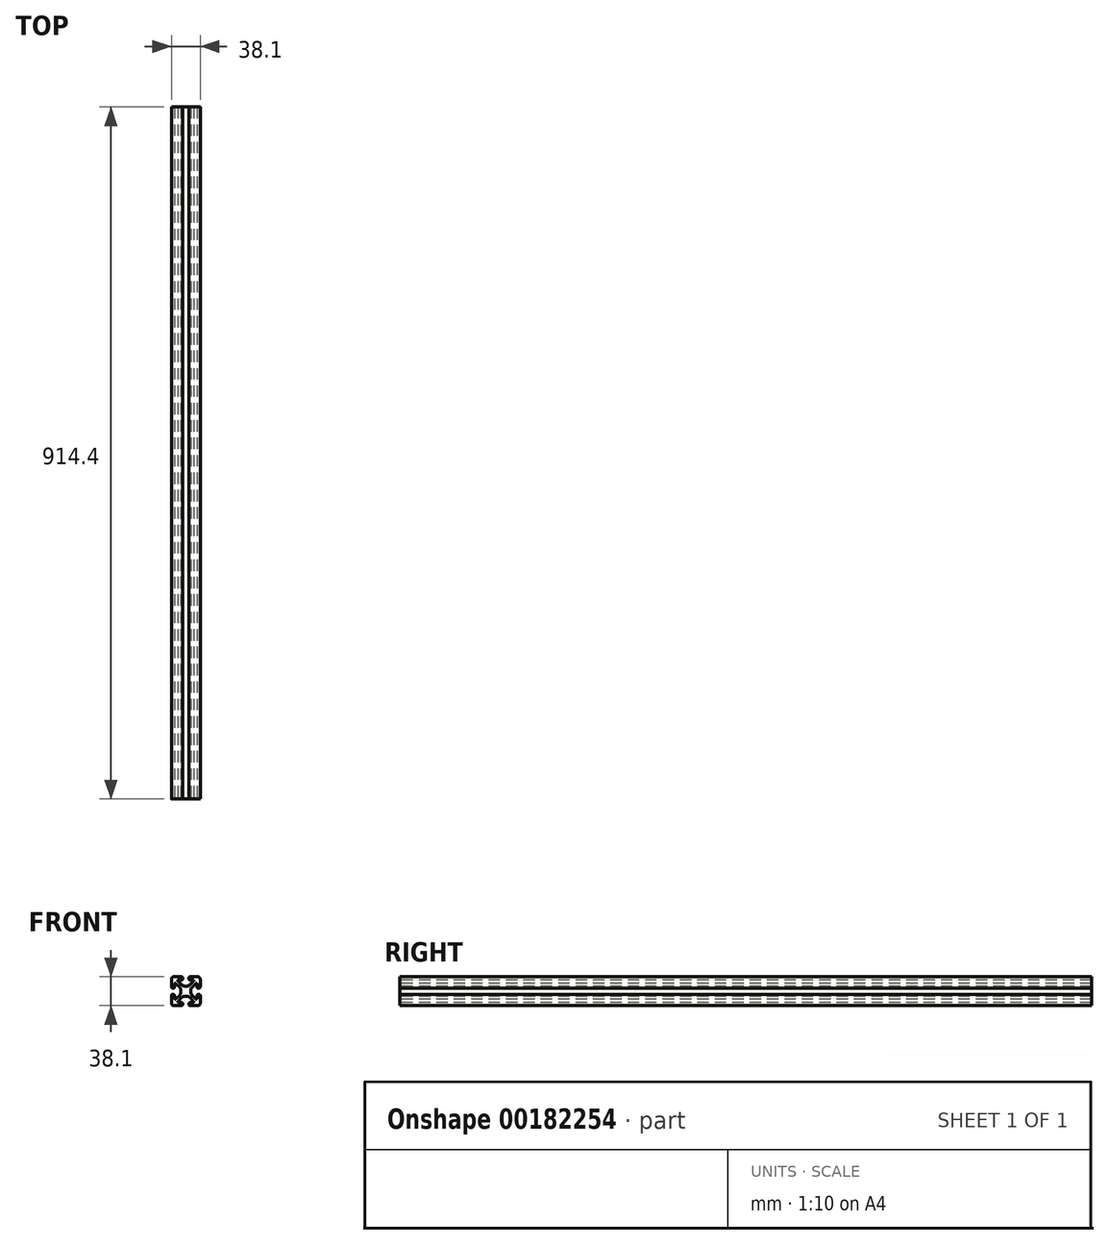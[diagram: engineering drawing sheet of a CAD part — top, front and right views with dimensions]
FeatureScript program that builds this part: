
annotation { "Feature Type Name" : "Feature", "Feature Type Description" : "" }
export const myFeature = defineFeature(function(context is Context, id is Id, definition is map)
    precondition{}
    {
        {
            var Q0;
            Q0=qCreatedBy(makeId("Front.planeOp"),FACE);
            var sketch = newSketch(context, id + "F0", { "sketchPlane" : qUnion([Q0])});
            skLineSegment(sketch, "E0", {"start": v(-16.03, 19.4) * mm, "end": v(-5.8, 19.4) * mm});
            skLineSegment(sketch, "E1.0", {"start": v(-19.2, 16.23) * mm, "end": v(-19.2, 5.99) * mm});
            skArc(sketch, "E2.0", {"start": v(-16.03, 19.4) * mm, "mid": v(-18.28, 18.47) * mm, "end": v(-19.2, 16.23) * mm});
            skArc(sketch, "E3.0", {"start": v(-19.2, 5.99) * mm, "mid": v(-18.75, 4.88) * mm, "end": v(-17.63, 4.41) * mm});
            skLineSegment(sketch, "E4.0", {"start": v(-17.63, 4.41) * mm, "end": v(-16.72, 4.41) * mm});
            skArc(sketch, "E5.0", {"start": v(-16.72, 4.41) * mm, "mid": v(-15.6, 4.88) * mm, "end": v(-15.15, 5.99) * mm});
            skLineSegment(sketch, "E6.0", {"start": v(-15.15, 5.99) * mm, "end": v(-15.15, 9.75) * mm});
            skArc(sketch, "E7.0", {"start": v(-15.15, 9.75) * mm, "mid": v(-14.89, 10.38) * mm, "end": v(-14.26, 10.64) * mm});
            skLineSegment(sketch, "E8.0", {"start": v(-14.26, 10.64) * mm, "end": v(-13.69, 10.64) * mm});
            skArc(sketch, "E9.0", {"start": v(-13.69, 10.64) * mm, "mid": v(-13.35, 10.57) * mm, "end": v(-13.06, 10.38) * mm});
            skLineSegment(sketch, "E10.0", {"start": v(-13.06, 10.38) * mm, "end": v(-8.42, 5.74) * mm});
            skArc(sketch, "E11.0", {"start": v(-8.42, 5.74) * mm, "mid": v(-7.4, 4.2) * mm, "end": v(-7.03, 2.38) * mm});
            skLineSegment(sketch, "E12.0", {"start": v(-7.03, 2.38) * mm, "end": v(-7.03, -1.68) * mm});
            skArc(sketch, "E13.0", {"start": v(-7.03, -1.68) * mm, "mid": v(-7.4, -3.5) * mm, "end": v(-8.42, -5.04) * mm});
            skLineSegment(sketch, "E14.0", {"start": v(-8.42, -5.04) * mm, "end": v(-13.06, -9.68) * mm});
            skArc(sketch, "E15.0", {"start": v(-13.06, -9.68) * mm, "mid": v(-13.35, -9.87) * mm, "end": v(-13.69, -9.94) * mm});
            skLineSegment(sketch, "E16.0", {"start": v(-13.69, -9.94) * mm, "end": v(-14.26, -9.94) * mm});
            skArc(sketch, "E17.0", {"start": v(-14.26, -9.94) * mm, "mid": v(-14.89, -9.68) * mm, "end": v(-15.15, -9.05) * mm});
            skLineSegment(sketch, "E18.0", {"start": v(-15.15, -9.05) * mm, "end": v(-15.15, -5.29) * mm});
            skArc(sketch, "E19.0", {"start": v(-15.15, -5.29) * mm, "mid": v(-15.6, -4.17) * mm, "end": v(-16.72, -3.71) * mm});
            skLineSegment(sketch, "E20.0", {"start": v(-16.72, -3.71) * mm, "end": v(-17.63, -3.71) * mm});
            skArc(sketch, "E21.0", {"start": v(-17.63, -3.71) * mm, "mid": v(-18.75, -4.17) * mm, "end": v(-19.2, -5.29) * mm});
            skLineSegment(sketch, "E22.0", {"start": v(-19.2, -5.29) * mm, "end": v(-19.2, -15.52) * mm});
            skArc(sketch, "E23.0", {"start": v(-19.2, -15.52) * mm, "mid": v(-18.28, -17.77) * mm, "end": v(-16.03, -18.7) * mm});
            skLineSegment(sketch, "E24.0", {"start": v(-16.03, -18.7) * mm, "end": v(-5.8, -18.7) * mm});
            skArc(sketch, "E25.0", {"start": v(-5.8, -18.7) * mm, "mid": v(-4.68, -18.24) * mm, "end": v(-4.22, -17.12) * mm});
            skLineSegment(sketch, "E26.0", {"start": v(-4.22, -17.12) * mm, "end": v(-4.22, -16.2) * mm});
            skArc(sketch, "E27.0", {"start": v(-4.22, -16.2) * mm, "mid": v(-4.68, -15.1) * mm, "end": v(-5.8, -14.64) * mm});
            skLineSegment(sketch, "E28.0", {"start": v(-5.8, -14.64) * mm, "end": v(-9.56, -14.64) * mm});
            skArc(sketch, "E29.0", {"start": v(-9.56, -14.64) * mm, "mid": v(-10.19, -14.37) * mm, "end": v(-10.45, -13.75) * mm});
            skLineSegment(sketch, "E30.0", {"start": v(-10.45, -13.75) * mm, "end": v(-10.45, -13.18) * mm});
            skArc(sketch, "E31.0", {"start": v(-10.45, -13.18) * mm, "mid": v(-10.38, -12.84) * mm, "end": v(-10.19, -12.55) * mm});
            skLineSegment(sketch, "E32.0", {"start": v(-10.19, -12.55) * mm, "end": v(-5.55, -7.91) * mm});
            skArc(sketch, "E33.0", {"start": v(-5.55, -7.91) * mm, "mid": v(-4, -6.88) * mm, "end": v(-2.19, -6.52) * mm});
            skLineSegment(sketch, "E34.0", {"start": v(-2.19, -6.52) * mm, "end": v(1.87, -6.52) * mm});
            skArc(sketch, "E35.0", {"start": v(1.87, -6.52) * mm, "mid": v(3.69, -6.88) * mm, "end": v(5.23, -7.91) * mm});
            skLineSegment(sketch, "E36.0", {"start": v(5.23, -7.91) * mm, "end": v(9.87, -12.55) * mm});
            skArc(sketch, "E37.0", {"start": v(9.87, -12.55) * mm, "mid": v(10.06, -12.84) * mm, "end": v(10.13, -13.18) * mm});
            skPoint(sketch, "E38.0", {"position": v(10.13, -13.75) * mm});
            skArc(sketch, "E39.0", {"start": v(10.13, -13.75) * mm, "mid": v(9.87, -14.37) * mm, "end": v(9.24, -14.64) * mm});
            skLineSegment(sketch, "E40.0", {"start": v(9.24, -14.64) * mm, "end": v(5.48, -14.64) * mm});
            skArc(sketch, "E41.0", {"start": v(5.48, -14.64) * mm, "mid": v(4.37, -15.1) * mm, "end": v(3.9, -16.2) * mm});
            skPoint(sketch, "E42.0", {"position": v(3.9, -17.12) * mm});
            skLineSegment(sketch, "E43.0", {"start": v(3.9, -16.2) * mm, "end": v(3.9, -17.12) * mm});
            skArc(sketch, "E44.0", {"start": v(3.9, -17.12) * mm, "mid": v(4.37, -18.24) * mm, "end": v(5.48, -18.7) * mm});
            skLineSegment(sketch, "E45.0", {"start": v(5.48, -18.7) * mm, "end": v(15.72, -18.7) * mm});
            skArc(sketch, "E46.0", {"start": v(15.72, -18.7) * mm, "mid": v(17.96, -17.77) * mm, "end": v(18.9, -15.52) * mm});
            skLineSegment(sketch, "E47.0", {"start": v(18.9, -15.52) * mm, "end": v(18.9, -5.29) * mm});
            skArc(sketch, "E48.0", {"start": v(18.9, -5.29) * mm, "mid": v(18.43, -4.17) * mm, "end": v(17.32, -3.71) * mm});
            skLineSegment(sketch, "E49.0", {"start": v(17.32, -3.71) * mm, "end": v(16.4, -3.71) * mm});
            skArc(sketch, "E50.0", {"start": v(16.4, -3.71) * mm, "mid": v(15.29, -4.17) * mm, "end": v(14.83, -5.29) * mm});
            skLineSegment(sketch, "E51.0", {"start": v(14.83, -5.29) * mm, "end": v(14.83, -9.05) * mm});
            skArc(sketch, "E52.0", {"start": v(14.83, -9.05) * mm, "mid": v(14.57, -9.68) * mm, "end": v(13.94, -9.94) * mm});
            skLineSegment(sketch, "E53.0", {"start": v(13.94, -9.94) * mm, "end": v(13.37, -9.94) * mm});
            skArc(sketch, "E54.0", {"start": v(13.37, -9.94) * mm, "mid": v(13.03, -9.87) * mm, "end": v(12.74, -9.68) * mm});
            skLineSegment(sketch, "E55.0", {"start": v(12.74, -9.68) * mm, "end": v(8.1, -5.04) * mm});
            skArc(sketch, "E56.0", {"start": v(8.1, -5.04) * mm, "mid": v(7.07, -3.5) * mm, "end": v(6.71, -1.68) * mm});
            skLineSegment(sketch, "E57.0", {"start": v(6.71, -1.68) * mm, "end": v(6.71, 2.38) * mm});
            skArc(sketch, "E58.0", {"start": v(6.71, 2.38) * mm, "mid": v(7.07, 4.2) * mm, "end": v(8.1, 5.74) * mm});
            skLineSegment(sketch, "E59.0", {"start": v(8.1, 5.74) * mm, "end": v(12.74, 10.38) * mm});
            skArc(sketch, "E60.0", {"start": v(12.74, 10.38) * mm, "mid": v(13.03, 10.57) * mm, "end": v(13.37, 10.64) * mm});
            skLineSegment(sketch, "E61.0", {"start": v(13.37, 10.64) * mm, "end": v(13.94, 10.64) * mm});
            skArc(sketch, "E62.0", {"start": v(13.94, 10.64) * mm, "mid": v(14.57, 10.38) * mm, "end": v(14.83, 9.75) * mm});
            skLineSegment(sketch, "E63.0", {"start": v(14.83, 9.75) * mm, "end": v(14.83, 5.99) * mm});
            skArc(sketch, "E64.0", {"start": v(14.83, 5.99) * mm, "mid": v(15.29, 4.88) * mm, "end": v(16.4, 4.41) * mm});
            skLineSegment(sketch, "E65.0", {"start": v(16.4, 4.41) * mm, "end": v(17.32, 4.41) * mm});
            skArc(sketch, "E66.0", {"start": v(17.32, 4.41) * mm, "mid": v(18.43, 4.88) * mm, "end": v(18.9, 5.99) * mm});
            skLineSegment(sketch, "E67.0", {"start": v(18.9, 5.99) * mm, "end": v(18.9, 16.23) * mm});
            skArc(sketch, "E68.0", {"start": v(18.9, 16.23) * mm, "mid": v(17.96, 18.47) * mm, "end": v(15.72, 19.4) * mm});
            skLineSegment(sketch, "E69.0", {"start": v(15.72, 19.4) * mm, "end": v(5.48, 19.4) * mm});
            skArc(sketch, "E70.0", {"start": v(5.48, 19.4) * mm, "mid": v(4.37, 18.94) * mm, "end": v(3.9, 17.83) * mm});
            skLineSegment(sketch, "E71.0", {"start": v(3.9, 17.83) * mm, "end": v(3.9, 16.91) * mm});
            skArc(sketch, "E72.0", {"start": v(3.9, 16.91) * mm, "mid": v(4.37, 15.8) * mm, "end": v(5.48, 15.34) * mm});
            skLineSegment(sketch, "E73.0", {"start": v(5.48, 15.34) * mm, "end": v(9.24, 15.34) * mm});
            skArc(sketch, "E74.0", {"start": v(9.24, 15.34) * mm, "mid": v(9.87, 15.08) * mm, "end": v(10.13, 14.45) * mm});
            skLineSegment(sketch, "E75.0", {"start": v(10.13, 14.45) * mm, "end": v(10.13, 13.88) * mm});
            skArc(sketch, "E76.0", {"start": v(10.13, 13.88) * mm, "mid": v(10.06, 13.54) * mm, "end": v(9.87, 13.25) * mm});
            skLineSegment(sketch, "E77.0", {"start": v(9.87, 13.25) * mm, "end": v(5.23, 8.61) * mm});
            skArc(sketch, "E78.0", {"start": v(-4.22, 17.83) * mm, "mid": v(-4.68, 18.94) * mm, "end": v(-5.8, 19.4) * mm});
            skLineSegment(sketch, "E79.0", {"start": v(-4.22, 16.91) * mm, "end": v(-4.22, 17.83) * mm});
            skArc(sketch, "E80.0", {"start": v(-5.8, 15.34) * mm, "mid": v(-4.68, 15.8) * mm, "end": v(-4.22, 16.91) * mm});
            skLineSegment(sketch, "E81.0", {"start": v(-9.56, 15.34) * mm, "end": v(-5.8, 15.34) * mm});
            skArc(sketch, "E82.0", {"start": v(-10.45, 14.45) * mm, "mid": v(-10.19, 15.08) * mm, "end": v(-9.56, 15.34) * mm});
            skLineSegment(sketch, "E83.0", {"start": v(-10.45, 13.88) * mm, "end": v(-10.45, 14.45) * mm});
            skArc(sketch, "E84.0", {"start": v(-10.19, 13.25) * mm, "mid": v(-10.38, 13.54) * mm, "end": v(-10.45, 13.88) * mm});
            skLineSegment(sketch, "E85.0", {"start": v(-5.55, 8.61) * mm, "end": v(-10.19, 13.25) * mm});
            skArc(sketch, "E86.0", {"start": v(-2.19, 7.22) * mm, "mid": v(-4, 7.58) * mm, "end": v(-5.55, 8.61) * mm});
            skLineSegment(sketch, "E87.0", {"start": v(1.87, 7.22) * mm, "end": v(-2.19, 7.22) * mm});
            skArc(sketch, "E88.0", {"start": v(5.23, 8.61) * mm, "mid": v(3.69, 7.58) * mm, "end": v(1.87, 7.22) * mm});
            skLineSegment(sketch, "E89.0", {"start": v(10.13, -13.18) * mm, "end": v(10.13, -13.75) * mm});
            skSolve(sketch);
        }
        {
            var Q0;
            Q0=qSketchRegion(id+"F0",true);
            extrude(context, id + "F1", {"entities" : qUnion([Q0]), "oppositeDirection" : true, "depth" : 914.4 * mm});
        }
    });
